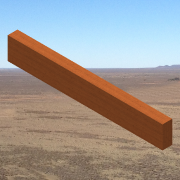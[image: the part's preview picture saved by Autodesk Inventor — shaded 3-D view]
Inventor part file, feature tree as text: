
AUTODESK INVENTOR PART (.ipt)
format: ipt  version: 2014 SP1 (Build 180222100, 222)  size: 126,976 bytes
history: native  units: in
note: dims shown in document units (in); Inventor stores cm internally (conversion verified against a paired STEP export)
features: extrude x1, sketch x1
ambient origin geometry x8: Origin, YZ Plane, XZ Plane, XY Plane, X Axis, Y Axis, Z Axis, Center Point
bodies: Solid1 (feature_tree)
feature tree (2):
  extrude  "Extrusion1"  Depth=3.5in
  sketch  "Sketch1"  dims[d0=1.5in d1=3.5in d2=24.0in d3=0.0in]
